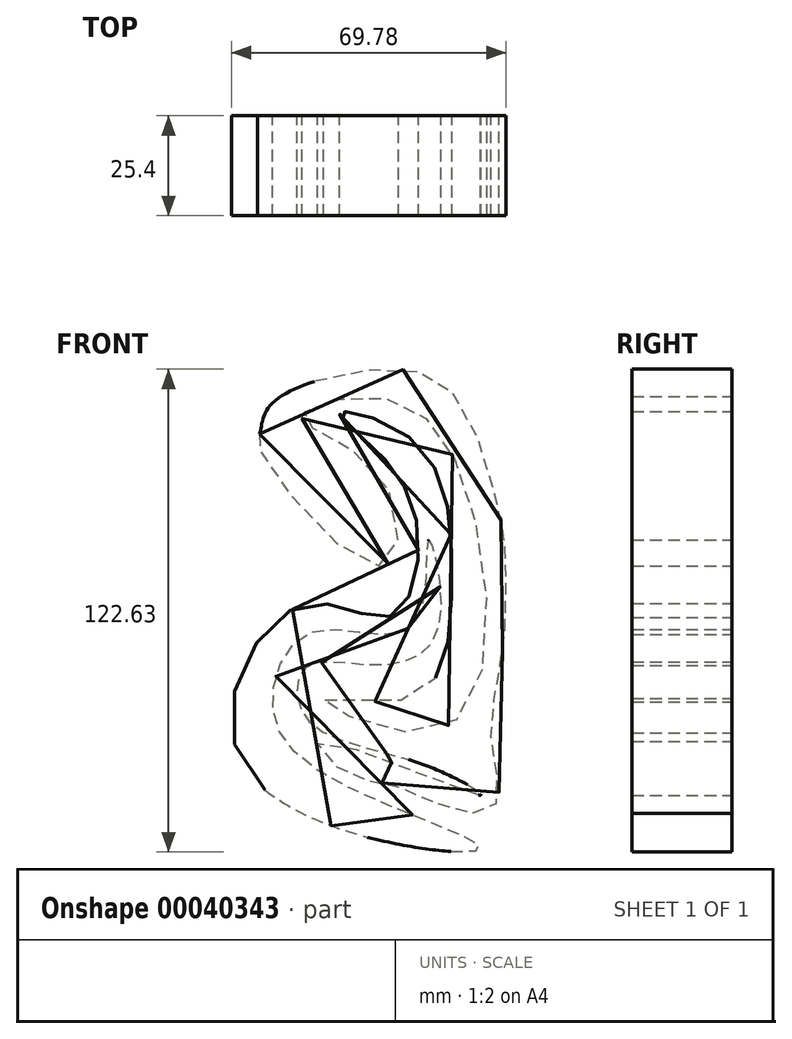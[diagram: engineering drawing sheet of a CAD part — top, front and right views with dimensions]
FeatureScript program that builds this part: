
annotation { "Feature Type Name" : "Feature", "Feature Type Description" : "" }
export const myFeature = defineFeature(function(context is Context, id is Id, definition is map)
    precondition{}
    {
        {
            var Q0;
            Q0=qCreatedBy(makeId("Front.planeOp"),FACE);
            var sketch = newSketch(context, id + "F0", { "sketchPlane" : qUnion([Q0])});
            skFitSpline(sketch, "E0", {"points": [v(-67.12, 54.93) * mm, v(-67.35, 51.44) * mm, v(-36.7, 21.48) * mm, v(-36.23, 44.01) * mm, v(-56.44, 59.34) * mm, v(-36.46, 64.22) * mm, v(-13.93, 38.67) * mm, v(-20.67, -19.86) * mm, v(-50.86, -12.66) * mm, v(-28.57, -11.96) * mm, v(-18.35, 16.14) * mm, v(-27.4, 52.6) * mm, v(-46.68, 60.27) * mm, v(-39.48, 52.6) * mm, v(-27.17, 32.17) * mm, v(-33.68, 8.7) * mm, v(-56.67, 11.26) * mm, v(-70.37, -30.54) * mm, v(-11.15, -50.51) * mm, v(-47.61, -33.33) * mm, v(-63.87, -13.35) * mm, v(-54.81, 4.3) * mm, v(-34.14, 4.06) * mm, v(-25.55, 11.96) * mm, v(-24.15, 27.99) * mm, v(-21.83, 5.46) * mm, v(-37.86, -3.83) * mm, v(-55.5, -4.53) * mm, v(-55.28, -17.3) * mm, v(-24.62, -29.38) * mm, v(-11.38, -36.81) * mm, v(-52.02, -23.34) * mm, v(-45.06, -31.24) * mm, v(-33.21, -34.26) * mm, v(-14.86, -41.22) * mm, v(-6.74, -38.44) * mm, v(-8.13, -24.73) * mm, v(-6.74, -7.78) * mm, v(-4.64, 8.7) * mm, v(-4.88, 27.06) * mm, v(-5.34, 30.54) * mm, v(-15.1, 61.2) * mm, v(-33.44, 71.42) * mm, v(-64.33, 62.36) * mm, v(-67.12, 54.93) * mm]});
            skSolve(sketch);
        }
        {
            var Q0;
            Q0=makeQuery(id+"F0.imprint","IMPRINT",FACE,{"disambiguationData":[TD([[makeQuery(id+"F0.imprint","IMPRINT",EDGE,{"derivedFrom":sQuery(id+"F0.wireOp",EDGE,"E0")}),1.0]])]});
            extrude(context, id + "F1", {"entities" : qUnion([Q0]), "depth" : 25.4 * mm});
        }
    });
